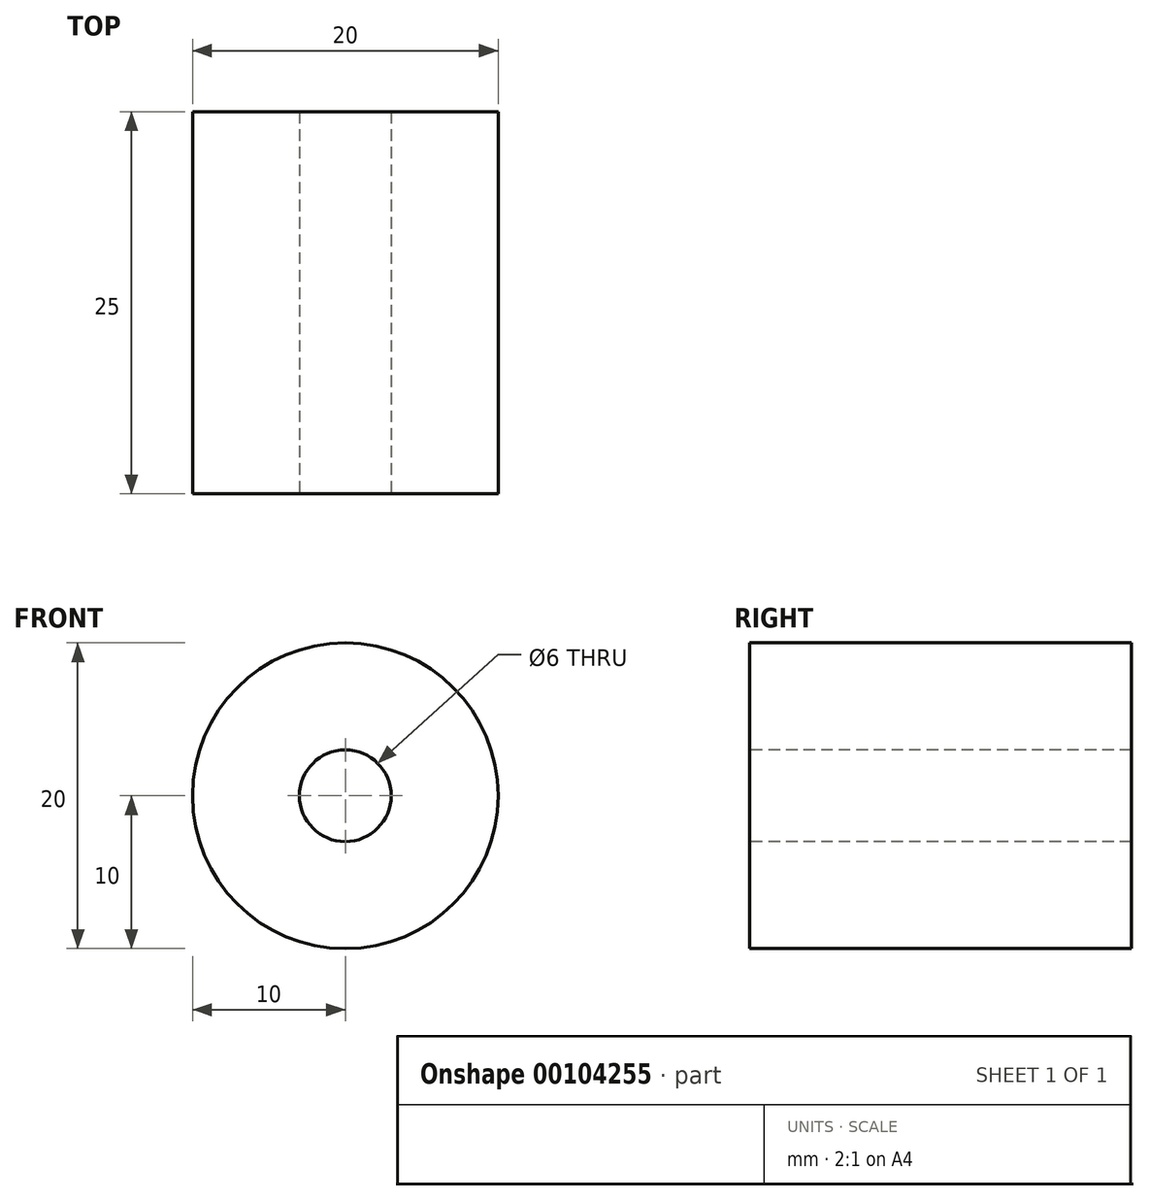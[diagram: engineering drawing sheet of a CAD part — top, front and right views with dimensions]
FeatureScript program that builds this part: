
annotation { "Feature Type Name" : "Feature", "Feature Type Description" : "" }
export const myFeature = defineFeature(function(context is Context, id is Id, definition is map)
    precondition{}
    {
        {
            var Q0;
            Q0=qCreatedBy(makeId("Front.planeOp"),FACE);
            var sketch = newSketch(context, id + "F0", { "sketchPlane" : qUnion([Q0])});
            skCircle(sketch, "E0", {"center": v(0, 0) * mm, "radius": 10 * mm});
            skSolve(sketch);
        }
        {
            var Q0;
            Q0=qSketchRegion(id+"F0",true);
            extrude(context, id + "F1", {"entities" : qUnion([Q0]), "depth" : 25 * mm});
        }
        {
            var Q0;
            Q0=makeQuery(id+"F1.opExtrude","CAP_FACE",FACE,{"disambiguationData":[OSD([sQuery(id+"F0.wireOp",EDGE,"E0")])],"isStart":false});
            var sketch = newSketch(context, id + "F2", { "sketchPlane" : qUnion([Q0])});
            skCircle(sketch, "E1", {"center": v(0, 0) * mm, "radius": 3 * mm});
            skSolve(sketch);
        }
        {
            var Q0;
            Q0 = qSketchRegion(id + "F2", true);
            extrude(context, id + "F3", {"entities" : qUnion([Q0]), "operationType" : NewBodyOperationType.REMOVE, "endBound" : BoundingType.THROUGH_ALL, "oppositeDirection" : true, "depth" : 25 * mm});
        }
    });
